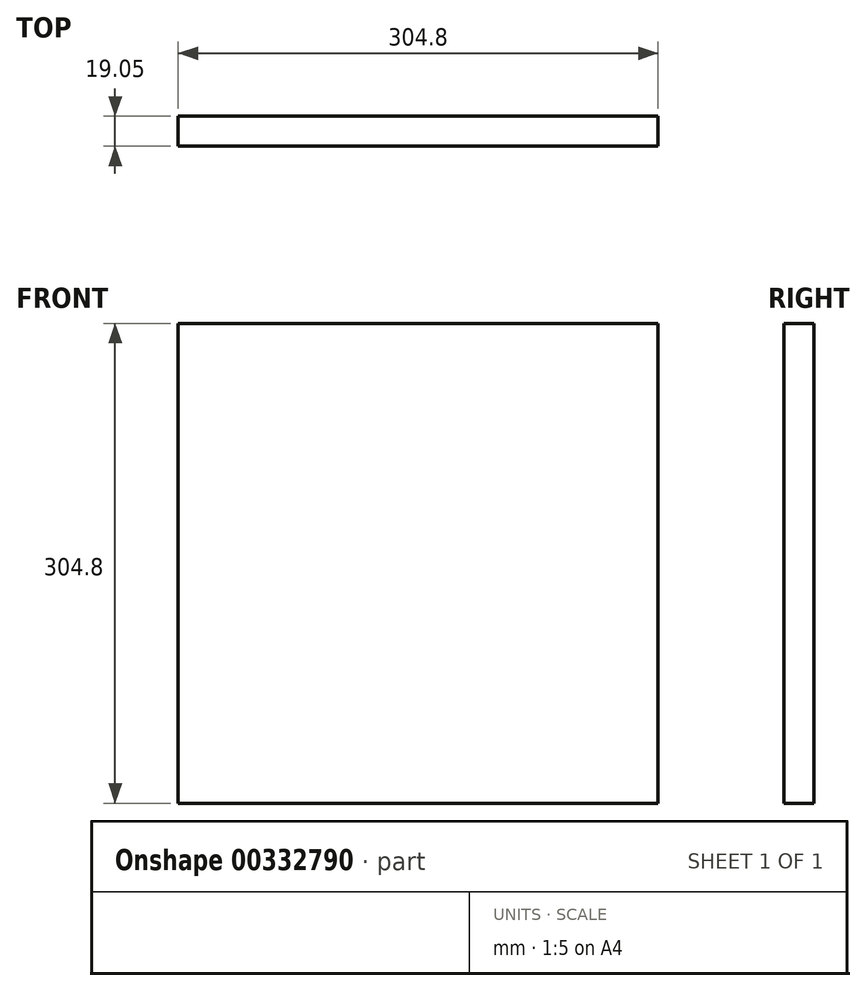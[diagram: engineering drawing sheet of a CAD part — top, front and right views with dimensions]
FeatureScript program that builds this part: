
annotation { "Feature Type Name" : "Feature", "Feature Type Description" : "" }
export const myFeature = defineFeature(function(context is Context, id is Id, definition is map)
    precondition{}
    {
        {
            var Q0;
            Q0=qCreatedBy(makeId("Front.planeOp"),FACE);
            var sketch = newSketch(context, id + "F0", { "sketchPlane" : qUnion([Q0])});
            skLineSegment(sketch, "E0.bottom", {"start": v(152.4, 152.4) * mm, "end": v(-152.4, 152.4) * mm});
            skLineSegment(sketch, "E0.top", {"start": v(152.4, -152.4) * mm, "end": v(-152.4, -152.4) * mm});
            skLineSegment(sketch, "E0.left", {"start": v(152.4, 152.4) * mm, "end": v(152.4, -152.4) * mm});
            skLineSegment(sketch, "E0.right", {"start": v(-152.4, 152.4) * mm, "end": v(-152.4, -152.4) * mm});
            skPoint(sketch, "E0.middle", {"position": v(0, 0) * mm});
            skSolve(sketch);
        }
        {
            var Q0;
            Q0 = qSketchRegion(id + "F0", true);
            extrude(context, id + "F1", {"entities" : qUnion([Q0]), "depth" : 19.05 * mm});
        }
    });
